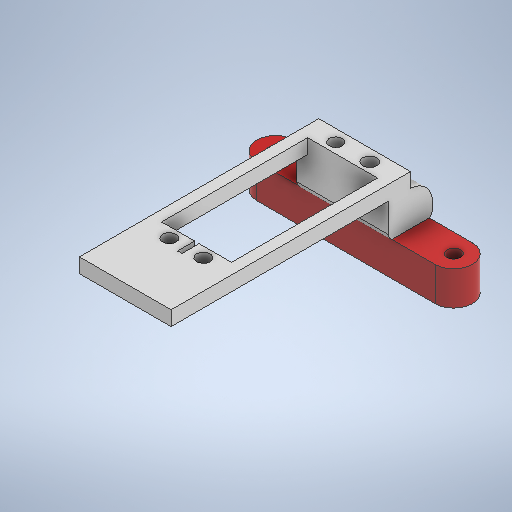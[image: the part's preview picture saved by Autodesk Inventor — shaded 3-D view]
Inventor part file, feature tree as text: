
AUTODESK INVENTOR PART (.ipt)
format: ipt  version: 2025.1 (Build 291241000, 241)  size: 340,480 bytes
history: native  units: in
note: dims shown in document units (in); Inventor stores cm internally (conversion verified against a paired STEP export)
features: extrude x5, sketch x5, fillet x2, other x1
ambient origin geometry x8: Origin, YZ Plane, XZ Plane, XY Plane, X Axis, Y Axis, Z Axis, Center Point
bodies: Solid1 (feature_tree)
feature tree (13):
  extrude  "Extrusion1"  Depth=0.3937in TaperAngle=0.0deg
  extrude  "Extrusion2"  Depth=0.5118in
  fillet  "Fillet1"  Radius=0.5732in
  extrude  "Extrusion3"  Depth=0.0787in
  extrude  "Extrusion4"  Depth=0.3937in TaperAngle=0.0deg
  fillet  "Fillet2"  Radius=0.1688in
  extrude  "Extrusion5"  Depth=0.126in
  sketch  "Sketch1"  dims[d0=0.4331in d1=0.4331in d2=0.3937in d3=0.0in]
  sketch  "Sketch2"  dims[d4=1.063in d5=0.5118in d6=0.5732in d7=0.0in]
  sketch  "Sketch3"  dims[d8=0.0787in d12=0.3346in]
  sketch  "Sketch4"  dims[d13=0.3346in d14=0.3937in d15=0.0in d16=0.1688in d17=0.0in]
  sketch  "Sketch5"  dims[d18=0.2662in d19=0.126in d20=2.5197in d21=0.126in d22=2.5197in d23=1.811in d24=0.3346in d25=0.1575in d26=0.3346in d27=0.1575in d28=0.2362in d29=0.2362in d30=0.0512in d32=0.1688in d33=0.0in d9=0.0344in d10=0.0in d11=0.0in]
  other  "Finish1"
